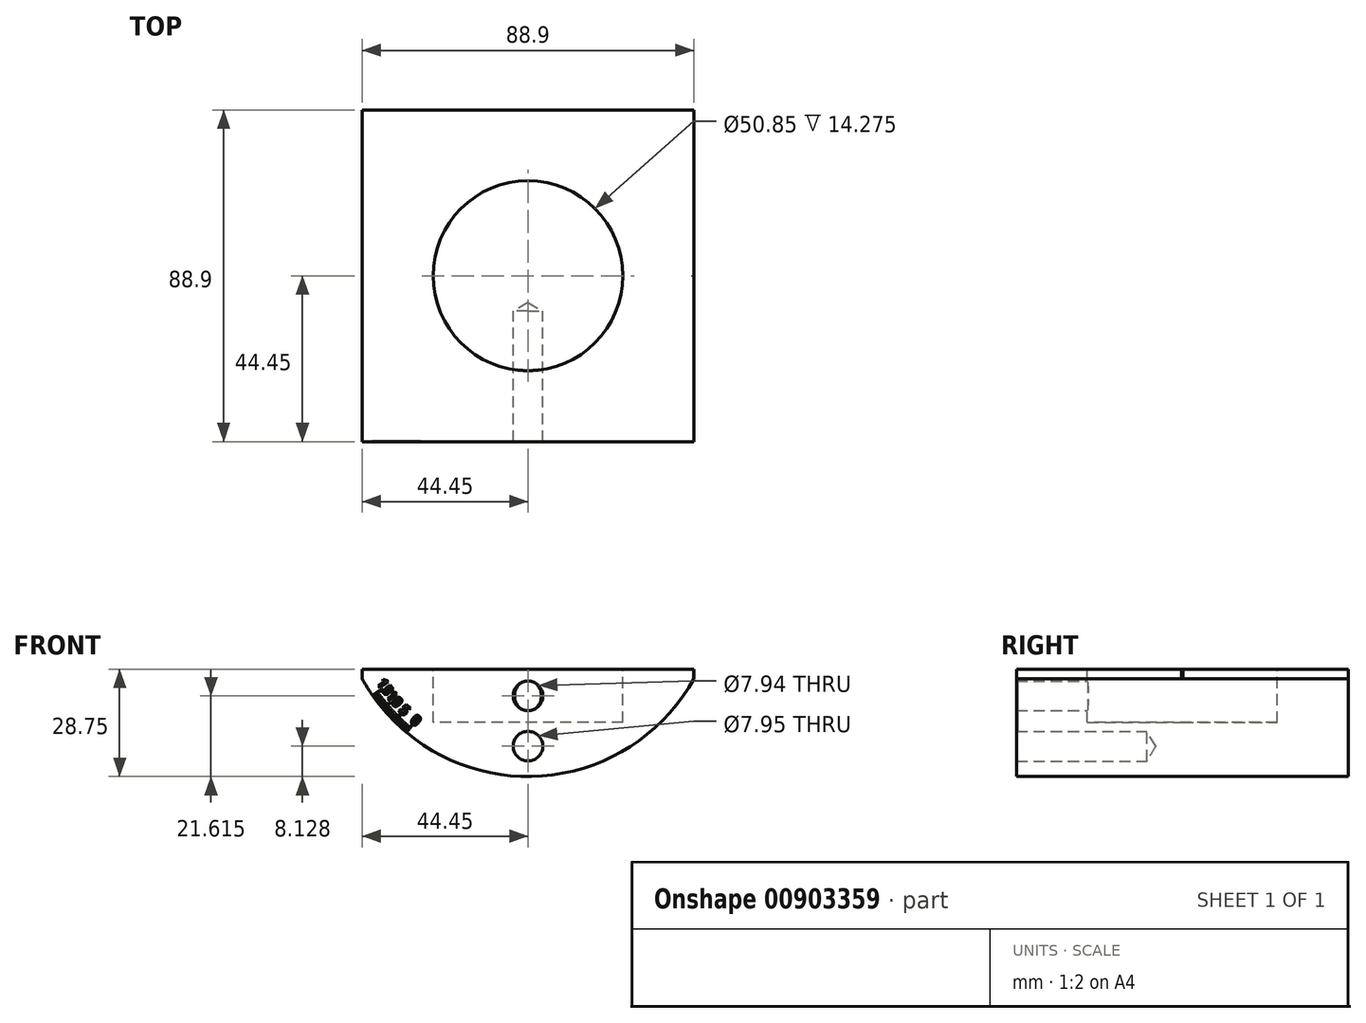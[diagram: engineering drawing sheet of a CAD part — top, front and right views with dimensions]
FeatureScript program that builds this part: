
annotation { "Feature Type Name" : "Feature", "Feature Type Description" : "" }
export const myFeature = defineFeature(function(context is Context, id is Id, definition is map)
    precondition{}
    {
        {
            var Q0;
            Q0=qCreatedBy(makeId("Front.planeOp"),FACE);
            var sketch = newSketch(context, id + "F0", { "sketchPlane" : qUnion([Q0])});
            skArc(sketch, "E0", {"start": v(-44.45, 26.2) * mm, "mid": v(0, 0) * mm, "end": v(44.45, 26.2) * mm});
            skLineSegment(sketch, "E1", {"start": v(-44.45, 28.75) * mm, "end": v(44.45, 28.75) * mm});
            skLineSegment(sketch, "E2", {"start": v(-44.45, 28.75) * mm, "end": v(-44.45, 26.2) * mm});
            skLineSegment(sketch, "E3", {"start": v(44.45, 28.75) * mm, "end": v(44.45, 26.2) * mm});
            skSolve(sketch);
        }
        {
            var Q0;
            Q0 = qSketchRegion(id + "F0", true);
            extrude(context, id + "F1", {"entities" : qUnion([Q0]), "depth" : 44.45 * mm, "offsetDistance" : 25.4 * mm, "hasSecondDirection" : true, "secondDirectionOppositeDirection" : true, "secondDirectionDepth" : 44.45 * mm});
        }
        {
            var Q0;
            Q0=makeQuery(id+"F1.opExtrude","SWEPT_FACE",FACE,{"disambiguationData":[OSD([sQuery(id+"F0.wireOp",EDGE,"E1")])]});
            cPlane(context, id + "F2", {"entities" : qUnion([Q0]), "cplaneType" : CPlaneType.OFFSET, "offset" : 0 * mm, "width" : 152.4 * mm, "height" : 152.4 * mm});
        }
        {
            var Q0;
            Q0=qCreatedBy(id+"F2.planeOp",FACE);
            var sketch = newSketch(context, id + "F3", { "sketchPlane" : qUnion([Q0])});
            skCircle(sketch, "E4", {"center": v(0, 0) * mm, "radius": 25.43 * mm});
            skSolve(sketch);
        }
        {
            var Q0;
            Q0=makeQuery(id+"F3.imprint","IMPRINT",FACE,{"disambiguationData":[TD([[makeQuery(id+"F3.imprint","IMPRINT",EDGE,{"derivedFrom":sQuery(id+"F3.wireOp",EDGE,"E4")}),1.0]])]});
            extrude(context, id + "F4", {"entities" : qUnion([Q0]), "operationType" : NewBodyOperationType.REMOVE, "oppositeDirection" : true, "depth" : 14.27 * mm, "offsetDistance" : 25.4 * mm});
        }
        {
            var Q0;
            Q0=makeQuery(id+"F1.opExtrude","CAP_FACE",FACE,{"disambiguationData":[OSD([sQuery(id+"F0.wireOp",EDGE,"E0"),sQuery(id+"F0.wireOp",EDGE,"E1"),sQuery(id+"F0.wireOp",EDGE,"E2"),sQuery(id+"F0.wireOp",EDGE,"E3")])],"isStart":false});
            cPlane(context, id + "F5", {"entities" : qUnion([Q0]), "cplaneType" : CPlaneType.OFFSET, "offset" : 0 * mm, "width" : 152.4 * mm, "height" : 152.4 * mm});
        }
        {
            var Q0;
            Q0=qCreatedBy(id+"F5.planeOp",FACE);
            var sketch = newSketch(context, id + "F6", { "sketchPlane" : qUnion([Q0])});
            skPoint(sketch, "E5", {"position": v(0, 21.62) * mm});
            skPoint(sketch, "E6", {"position": v(0, 8.13) * mm});
            skSolve(sketch);
        }
        {
            var Q0;
            Q0=sQuery(id+"F6.wireOp",VERTEX,"E5");
            var Q1;
            Q1=makeQuery(id+"F1.opExtrude","SWEPT_BODY",BODY,{"disambiguationData":[OSD([sQuery(id+"F0.wireOp",EDGE,"E0"),sQuery(id+"F0.wireOp",EDGE,"E1"),sQuery(id+"F0.wireOp",EDGE,"E2"),sQuery(id+"F0.wireOp",EDGE,"E3")])]});
            hole(context, id + "F7", {"style" : HoleStyle.SIMPLE, "endStyle" : HoleEndStyle.BLIND, "standardTappedOrClearance" : lookupTablePath({ "standard" : "ANSI", "engagement" : "75%", "pitch" : "16 tpi", "size" : "3/8", "type" : "Tapped" }), "standardBlindInLast" : lookupTablePath({ "standard" : "ANSI", "engagement" : "75%", "pitch" : "16 tpi", "size" : "3/8", "type" : "Tapped" }), "holeDiameter" : 7.94 * mm, "majorDiameter" : 9.52 * mm, "showTappedDepth" : true, "holeDepth" : 19.06 * mm, "tappedDepth" : 14.3 * mm, "tapClearance" : 3, "locations" : qUnion([Q0]), "scope" : qUnion([Q1]), "startStyle" : HoleStartStyle.PART});
        }
        {
            var Q0;
            Q0=sQuery(id+"F6.wireOp",VERTEX,"E6");
            var Q1;
            Q1=makeQuery(id+"F1.opExtrude","SWEPT_BODY",BODY,{"disambiguationData":[OSD([sQuery(id+"F0.wireOp",EDGE,"E0"),sQuery(id+"F0.wireOp",EDGE,"E1"),sQuery(id+"F0.wireOp",EDGE,"E2"),sQuery(id+"F0.wireOp",EDGE,"E3")])]});
            hole(context, id + "F8", {"style" : HoleStyle.SIMPLE, "endStyle" : HoleEndStyle.BLIND, "standardTappedOrClearance" : lookupTablePath({ "standard" : "ANSI", "size" : "19/64 (0.3)", "type" : "Drilled" }), "standardBlindInLast" : lookupTablePath({ "standard" : "ANSI", "size" : "19/64", "type" : "Drilled" }), "holeDiameter" : 19 / 1625.6 * mm, "majorDiameter" : 9.52 * mm, "holeDepth" : 17.48 * mm, "tappedDepth" : 14.3 * mm, "tapClearance" : 3, "locations" : qUnion([Q0]), "scope" : qUnion([Q1]), "startStyle" : HoleStartStyle.PART});
        }
        {
            var Q0;
            Q0=sQuery(id+"F6.wireOp",VERTEX,"E6");
            var Q1;
            Q1=makeQuery(id+"F1.opExtrude","SWEPT_BODY",BODY,{"disambiguationData":[OSD([sQuery(id+"F0.wireOp",EDGE,"E0"),sQuery(id+"F0.wireOp",EDGE,"E1"),sQuery(id+"F0.wireOp",EDGE,"E2"),sQuery(id+"F0.wireOp",EDGE,"E3")])]});
            hole(context, id + "F9", {"style" : HoleStyle.SIMPLE, "endStyle" : HoleEndStyle.BLIND, "holeDiameter" : 7.95 * mm, "majorDiameter" : 6.35 * mm, "holeDepth" : 17.48 * mm, "tappedDepth" : 14.33 * mm, "tapClearance" : 3, "locations" : qUnion([Q0]), "scope" : qUnion([Q1]), "startStyle" : HoleStartStyle.PART});
        }
        {
            var Q0;
            Q0=makeQuery(id+"F1.opExtrude","CAP_FACE",FACE,{"disambiguationData":[OSD([sQuery(id+"F0.wireOp",EDGE,"E0"),sQuery(id+"F0.wireOp",EDGE,"E1"),sQuery(id+"F0.wireOp",EDGE,"E2"),sQuery(id+"F0.wireOp",EDGE,"E3")])],"isStart":false});
            cPlane(context, id + "F10", {"entities" : qUnion([Q0]), "cplaneType" : CPlaneType.OFFSET, "offset" : 0 * mm, "width" : 152.4 * mm, "height" : 152.4 * mm});
        }
        {
            var Q0;
            Q0=qCreatedBy(id+"F10.planeOp",FACE);
            var sketch = newSketch(context, id + "F11", { "sketchPlane" : qUnion([Q0])});
            skText(sketch, "E7", { "text": "0", "fontName": "OpenSans-Bold.ttf"});
            skLineSegment(sketch, "E8", {"start": v(0, -3.39) * mm, "end": v(0, 47.41) * mm, "construction": true});
            skArc(sketch, "E9.0.3", {"start": v(-44.45, 26.2) * mm, "mid": v(0, 0) * mm, "end": v(44.45, 26.2) * mm, "construction": true});
            skLineSegment(sketch, "E10.0.0", {"start": v(44.45, 26.2) * mm, "end": v(44.45, 39.69) * mm, "construction": true});
            skArc(sketch, "E10.0.3", {"start": v(-44.45, 26.2) * mm, "mid": v(0, 0) * mm, "end": v(44.45, 26.2) * mm});
            skPoint(sketch, "E11.center", {"position": v(0, 47.41) * mm});
            skArc(sketch, "E12.0", {"start": v(-40.3, 22.58) * mm, "mid": v(2.6, 1.67) * mm, "end": v(43.05, 26.98) * mm, "construction": true});
            skArc(sketch, "E13.0", {"start": v(-39.68, 23.02) * mm, "mid": v(-35.71, 18.08) * mm, "end": v(-31.14, 13.7) * mm, "construction": true});
            skLineSegment(sketch, "E14.trimOffspring", {"start": v(-31.14, 13.7) * mm, "end": v(-32.65, 11.88) * mm, "construction": true});
            skLineSegment(sketch, "E15.trimOffspring", {"start": v(-31.14, 13.7) * mm, "end": v(-32.65, 11.88) * mm});
            skLineSegment(sketch, "E16.trimOffspring", {"start": v(-32.28, 13.67) * mm, "end": v(-33.33, 12.46) * mm});
            skLineSegment(sketch, "E17.trimOffspring", {"start": v(-32.92, 14.24) * mm, "end": v(-34, 13.05) * mm, "construction": true});
            skLineSegment(sketch, "E18.trimOffspring", {"start": v(-33.55, 14.82) * mm, "end": v(-34.65, 13.65) * mm, "construction": true});
            skLineSegment(sketch, "E19.trimOffspring", {"start": v(-34.18, 15.4) * mm, "end": v(-35.29, 14.26) * mm, "construction": true});
            skLineSegment(sketch, "E20.trimOffspring", {"start": v(-34.25, 16.55) * mm, "end": v(-35.92, 14.88) * mm, "construction": true});
            skLineSegment(sketch, "E21.trimOffspring", {"start": v(-35.4, 16.62) * mm, "end": v(-36.54, 15.51) * mm, "construction": true});
            skLineSegment(sketch, "E22.trimOffspring", {"start": v(-35.98, 17.25) * mm, "end": v(-37.15, 16.15) * mm, "construction": true});
            skLineSegment(sketch, "E23.trimOffspring", {"start": v(-36.56, 17.88) * mm, "end": v(-37.75, 16.8) * mm, "construction": true});
            skLineSegment(sketch, "E24.trimOffspring", {"start": v(-37.13, 18.52) * mm, "end": v(-38.34, 17.47) * mm, "construction": true});
            skLineSegment(sketch, "E25.trimOffspring", {"start": v(-38.24, 19.84) * mm, "end": v(-39.48, 18.83) * mm, "construction": true});
            skLineSegment(sketch, "E26.trimOffspring", {"start": v(-38.77, 20.5) * mm, "end": v(-40.03, 19.52) * mm, "construction": true});
            skLineSegment(sketch, "E27.trimOffspring", {"start": v(-39.3, 21.2) * mm, "end": v(-40.57, 20.23) * mm, "construction": true});
            skLineSegment(sketch, "E28.trimOffspring", {"start": v(-39.8, 21.88) * mm, "end": v(-41.1, 20.94) * mm, "construction": true});
            skLineSegment(sketch, "E29.trimOffspring", {"start": v(-39.68, 23.02) * mm, "end": v(-41.61, 21.66) * mm, "construction": true});
            skLineSegment(sketch, "E30.trimOffspring", {"start": v(-37.1, 19.66) * mm, "end": v(-38.92, 18.15) * mm, "construction": true});
            skLineSegment(sketch, "E31.trimOffspring", {"start": v(-39.68, 23.02) * mm, "end": v(-41.61, 21.66) * mm});
            skArc(sketch, "E32.0.startCap", {"start": v(-32.37, 13.75) * mm, "mid": v(-32.2, 13.76) * mm, "end": v(-32.18, 13.59) * mm});
            skArc(sketch, "E32.0.endCap", {"start": v(-33.23, 12.38) * mm, "mid": v(-33.41, 12.36) * mm, "end": v(-33.42, 12.54) * mm});
            skLineSegment(sketch, "E32.0.left", {"start": v(-32.18, 13.59) * mm, "end": v(-33.23, 12.38) * mm});
            skLineSegment(sketch, "E32.0.right", {"start": v(-32.37, 13.75) * mm, "end": v(-33.42, 12.54) * mm});
            skArc(sketch, "E33.0.startCap", {"start": v(-31.23, 13.78) * mm, "mid": v(-31.05, 13.8) * mm, "end": v(-31.04, 13.61) * mm});
            skArc(sketch, "E33.0.endCap", {"start": v(-32.56, 11.8) * mm, "mid": v(-32.74, 11.79) * mm, "end": v(-32.75, 11.97) * mm});
            skLineSegment(sketch, "E33.0.left", {"start": v(-31.04, 13.61) * mm, "end": v(-32.56, 11.8) * mm});
            skLineSegment(sketch, "E33.0.right", {"start": v(-31.23, 13.78) * mm, "end": v(-32.75, 11.97) * mm});
            skArc(sketch, "E34.0.startCap", {"start": v(-33.02, 14.32) * mm, "mid": v(-32.84, 14.33) * mm, "end": v(-32.83, 14.15) * mm});
            skArc(sketch, "E34.0.endCap", {"start": v(-33.9, 12.96) * mm, "mid": v(-34.08, 12.95) * mm, "end": v(-34.09, 13.13) * mm});
            skLineSegment(sketch, "E34.0.left", {"start": v(-32.83, 14.15) * mm, "end": v(-33.9, 12.96) * mm});
            skLineSegment(sketch, "E34.0.right", {"start": v(-33.02, 14.32) * mm, "end": v(-34.09, 13.13) * mm});
            skArc(sketch, "E35.0.startCap", {"start": v(-33.65, 14.9) * mm, "mid": v(-33.47, 14.91) * mm, "end": v(-33.46, 14.73) * mm});
            skArc(sketch, "E35.0.endCap", {"start": v(-34.55, 13.56) * mm, "mid": v(-34.73, 13.55) * mm, "end": v(-34.74, 13.73) * mm});
            skLineSegment(sketch, "E35.0.left", {"start": v(-33.46, 14.73) * mm, "end": v(-34.55, 13.56) * mm});
            skLineSegment(sketch, "E35.0.right", {"start": v(-33.65, 14.9) * mm, "end": v(-34.74, 13.73) * mm});
            skArc(sketch, "E36.0.startCap", {"start": v(-34.27, 15.5) * mm, "mid": v(-34.09, 15.5) * mm, "end": v(-34.09, 15.32) * mm});
            skArc(sketch, "E36.0.endCap", {"start": v(-35.2, 14.17) * mm, "mid": v(-35.38, 14.17) * mm, "end": v(-35.38, 14.35) * mm});
            skLineSegment(sketch, "E36.0.left", {"start": v(-34.09, 15.32) * mm, "end": v(-35.2, 14.17) * mm});
            skLineSegment(sketch, "E36.0.right", {"start": v(-34.27, 15.5) * mm, "end": v(-35.38, 14.35) * mm});
            skArc(sketch, "E37.0.startCap", {"start": v(-34.34, 16.64) * mm, "mid": v(-34.16, 16.64) * mm, "end": v(-34.16, 16.46) * mm});
            skArc(sketch, "E37.0.endCap", {"start": v(-35.83, 14.79) * mm, "mid": v(-36.01, 14.79) * mm, "end": v(-36.01, 14.97) * mm});
            skLineSegment(sketch, "E37.0.left", {"start": v(-34.16, 16.46) * mm, "end": v(-35.83, 14.79) * mm});
            skLineSegment(sketch, "E37.0.right", {"start": v(-34.34, 16.64) * mm, "end": v(-36.01, 14.97) * mm});
            skArc(sketch, "E37.1.startCap", {"start": v(-35.48, 16.71) * mm, "mid": v(-35.3, 16.71) * mm, "end": v(-35.3, 16.53) * mm});
            skArc(sketch, "E37.1.endCap", {"start": v(-36.45, 15.42) * mm, "mid": v(-36.63, 15.42) * mm, "end": v(-36.63, 15.6) * mm});
            skLineSegment(sketch, "E37.1.left", {"start": v(-35.3, 16.53) * mm, "end": v(-36.45, 15.42) * mm});
            skLineSegment(sketch, "E37.1.right", {"start": v(-35.48, 16.71) * mm, "end": v(-36.63, 15.6) * mm});
            skArc(sketch, "E37.2.startCap", {"start": v(-36.07, 17.34) * mm, "mid": v(-35.89, 17.33) * mm, "end": v(-35.9, 17.15) * mm});
            skArc(sketch, "E37.2.endCap", {"start": v(-37.07, 16.06) * mm, "mid": v(-37.25, 16.07) * mm, "end": v(-37.24, 16.25) * mm});
            skLineSegment(sketch, "E37.2.left", {"start": v(-35.9, 17.15) * mm, "end": v(-37.07, 16.06) * mm});
            skLineSegment(sketch, "E37.2.right", {"start": v(-36.07, 17.34) * mm, "end": v(-37.24, 16.25) * mm});
            skArc(sketch, "E37.3.startCap", {"start": v(-36.65, 17.97) * mm, "mid": v(-36.47, 17.96) * mm, "end": v(-36.48, 17.78) * mm});
            skArc(sketch, "E37.3.endCap", {"start": v(-37.67, 16.71) * mm, "mid": v(-37.85, 16.72) * mm, "end": v(-37.84, 16.9) * mm});
            skLineSegment(sketch, "E37.3.left", {"start": v(-36.48, 17.78) * mm, "end": v(-37.67, 16.71) * mm});
            skLineSegment(sketch, "E37.3.right", {"start": v(-36.65, 17.97) * mm, "end": v(-37.84, 16.9) * mm});
            skArc(sketch, "E37.4.startCap", {"start": v(-37.21, 18.62) * mm, "mid": v(-37.04, 18.6) * mm, "end": v(-37.05, 18.43) * mm});
            skArc(sketch, "E37.4.endCap", {"start": v(-38.26, 17.38) * mm, "mid": v(-38.44, 17.39) * mm, "end": v(-38.42, 17.57) * mm});
            skLineSegment(sketch, "E37.4.left", {"start": v(-37.05, 18.43) * mm, "end": v(-38.26, 17.38) * mm});
            skLineSegment(sketch, "E37.4.right", {"start": v(-37.21, 18.62) * mm, "end": v(-38.42, 17.57) * mm});
            skArc(sketch, "E37.5.startCap", {"start": v(-37.19, 19.76) * mm, "mid": v(-37, 19.75) * mm, "end": v(-37.02, 19.57) * mm});
            skArc(sketch, "E37.5.endCap", {"start": v(-38.83, 18.05) * mm, "mid": v(-39.01, 18.06) * mm, "end": v(-39, 18.24) * mm});
            skLineSegment(sketch, "E37.5.left", {"start": v(-37.02, 19.57) * mm, "end": v(-38.83, 18.05) * mm});
            skLineSegment(sketch, "E37.5.right", {"start": v(-37.19, 19.76) * mm, "end": v(-39, 18.24) * mm});
            skArc(sketch, "E37.6.startCap", {"start": v(-38.32, 19.94) * mm, "mid": v(-38.14, 19.92) * mm, "end": v(-38.16, 19.74) * mm});
            skArc(sketch, "E37.6.endCap", {"start": v(-39.4, 18.73) * mm, "mid": v(-39.58, 18.75) * mm, "end": v(-39.56, 18.93) * mm});
            skLineSegment(sketch, "E37.6.left", {"start": v(-38.16, 19.74) * mm, "end": v(-39.4, 18.73) * mm});
            skLineSegment(sketch, "E37.6.right", {"start": v(-38.32, 19.94) * mm, "end": v(-39.56, 18.93) * mm});
            skArc(sketch, "E37.7.startCap", {"start": v(-38.85, 20.6) * mm, "mid": v(-38.67, 20.59) * mm, "end": v(-38.7, 20.4) * mm});
            skArc(sketch, "E37.7.endCap", {"start": v(-39.95, 19.42) * mm, "mid": v(-40.13, 19.45) * mm, "end": v(-40.1, 19.62) * mm});
            skLineSegment(sketch, "E37.7.left", {"start": v(-38.7, 20.4) * mm, "end": v(-39.95, 19.42) * mm});
            skLineSegment(sketch, "E37.7.right", {"start": v(-38.85, 20.6) * mm, "end": v(-40.1, 19.62) * mm});
            skArc(sketch, "E37.8.startCap", {"start": v(-39.37, 21.3) * mm, "mid": v(-39.2, 21.27) * mm, "end": v(-39.22, 21.09) * mm});
            skArc(sketch, "E37.8.endCap", {"start": v(-40.5, 20.13) * mm, "mid": v(-40.67, 20.15) * mm, "end": v(-40.65, 20.33) * mm});
            skLineSegment(sketch, "E37.8.left", {"start": v(-39.22, 21.09) * mm, "end": v(-40.5, 20.13) * mm});
            skLineSegment(sketch, "E37.8.right", {"start": v(-39.37, 21.3) * mm, "end": v(-40.65, 20.33) * mm});
            skArc(sketch, "E37.9.startCap", {"start": v(-39.88, 21.98) * mm, "mid": v(-39.7, 21.96) * mm, "end": v(-39.73, 21.78) * mm});
            skArc(sketch, "E37.9.endCap", {"start": v(-41.02, 20.84) * mm, "mid": v(-41.2, 20.87) * mm, "end": v(-41.17, 21.04) * mm});
            skLineSegment(sketch, "E37.9.left", {"start": v(-39.73, 21.78) * mm, "end": v(-41.02, 20.84) * mm});
            skLineSegment(sketch, "E37.9.right", {"start": v(-39.88, 21.98) * mm, "end": v(-41.17, 21.04) * mm});
            skArc(sketch, "E37.10.startCap", {"start": v(-39.75, 23.12) * mm, "mid": v(-39.57, 23.1) * mm, "end": v(-39.6, 22.91) * mm});
            skArc(sketch, "E37.10.endCap", {"start": v(-41.54, 21.56) * mm, "mid": v(-41.72, 21.59) * mm, "end": v(-41.69, 21.77) * mm});
            skLineSegment(sketch, "E37.10.left", {"start": v(-39.6, 22.91) * mm, "end": v(-41.54, 21.56) * mm});
            skLineSegment(sketch, "E37.10.right", {"start": v(-39.75, 23.12) * mm, "end": v(-41.69, 21.77) * mm});
            skLineSegment(sketch, "E38", {"start": v(-31.14, 13.7) * mm, "end": v(-30.9, 13.99) * mm, "construction": true});
            skLineSegment(sketch, "E39", {"start": v(-34.25, 16.55) * mm, "end": v(-33.98, 16.82) * mm, "construction": true});
            skText(sketch, "E40", { "text": "5", "fontName": "OpenSans-Bold.ttf"});
            skText(sketch, "E41", { "text": "10", "fontName": "OpenSans-Bold.ttf"});
            skLineSegment(sketch, "E42", {"start": v(-37.1, 19.66) * mm, "end": v(-36.81, 19.9) * mm});
            skText(sketch, "E43", { "text": "15", "fontName": "OpenSans-Bold.ttf"});
            skLineSegment(sketch, "E44", {"start": v(-39.68, 23.02) * mm, "end": v(-39.37, 23.24) * mm});
            const initialGuessF11  = {"E7": [-0.03177, 0.01473, 0.76604, -0.64279, 0.00277], "E40": [-0.03478, 0.01762, 0.7071, -0.7071, 0.00277], "E41": [-0.03826, 0.02163, 0.64279, -0.76604, 0.00277], "E43": [-0.04065, 0.02507, 0.57358, -0.81915, 0.00277]};
            skSetInitialGuess(sketch, initialGuessF11);
            skSolve(sketch);
        }
        {
            var Q0;
            Q0 = qSketchRegion(id + "F11", true);
            extrude(context, id + "F12", {"entities" : qUnion([Q0]), "operationType" : NewBodyOperationType.REMOVE, "oppositeDirection" : true, "depth" : 0.25 * mm, "offsetDistance" : 25.4 * mm});
        }
        {
            var Q0;
            Q0=qCreatedBy(makeId("Front.planeOp"),FACE);
            cPlane(context, id + "F13", {"entities" : qUnion([Q0]), "cplaneType" : CPlaneType.OFFSET, "offset" : 0 * mm, "width" : 152.4 * mm, "height" : 152.4 * mm});
        }
        {
            var Q0;
            Q0=qCreatedBy(id+"F13.planeOp",FACE);
            var sketch = newSketch(context, id + "F14", { "sketchPlane" : qUnion([Q0])});
            skLineSegment(sketch, "E45", {"start": v(0, 0) * mm, "end": v(0, 80.44) * mm, "construction": true});
            skSolve(sketch);
        }
        {
            var Q0;
            Q0=makeQuery(id+"F1.opExtrude","SWEPT_FACE",FACE,{"disambiguationData":[OSD([sQuery(id+"F0.wireOp",EDGE,"E3")])]});
            cPlane(context, id + "F15", {"entities" : qUnion([Q0]), "cplaneType" : CPlaneType.OFFSET, "offset" : 0 * mm, "width" : 152.4 * mm, "height" : 152.4 * mm});
        }
        {
            var Q0;
            Q0=qCreatedBy(id+"F15.planeOp",FACE);
            var sketch = newSketch(context, id + "F16", { "sketchPlane" : qUnion([Q0])});
            skPoint(sketch, "E46.0", {"position": v(0, 28.75) * mm});
            skPoint(sketch, "E46.1", {"position": v(0, 26.2) * mm});
            skLineSegment(sketch, "E47", {"start": v(0, 26.2) * mm, "end": v(0, 28.75) * mm});
            skArc(sketch, "E48.0.endCap", {"start": v(-0.13, 28.75) * mm, "mid": v(0, 28.88) * mm, "end": v(0.13, 28.75) * mm});
            skLineSegment(sketch, "E48.0.left", {"start": v(-0.13, 26.2) * mm, "end": v(-0.13, 28.75) * mm});
            skLineSegment(sketch, "E48.0.right", {"start": v(0.13, 26.2) * mm, "end": v(0.13, 28.75) * mm});
            skLineSegment(sketch, "E49.0", {"start": v(-0.13, 26.2) * mm, "end": v(0.13, 26.2) * mm});
            skPoint(sketch, "E50.orphan", {"position": v(-44.45, 26.2) * mm});
            skPoint(sketch, "E51.orphan", {"position": v(44.45, 26.2) * mm});
            skSolve(sketch);
        }
        {
            var Q0;
            Q0 = qSketchRegion(id + "F16", true);
            extrude(context, id + "F17", {"entities" : qUnion([Q0]), "operationType" : NewBodyOperationType.REMOVE, "oppositeDirection" : true, "depth" : 0.25 * mm, "offsetDistance" : 25.4 * mm});
        }
    });
